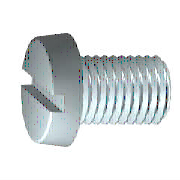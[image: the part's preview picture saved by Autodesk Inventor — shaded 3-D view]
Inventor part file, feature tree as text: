
AUTODESK INVENTOR PART (.ipt)
format: ipt  version: 2015 (Build 190159000, 159)  size: 181,248 bytes
history: native  units: mm (DEFAULTED — no unit token found)
features: sketch x2, extrude x1, plane x1
ambient origin geometry x7: Origin, YZ Plane, XZ Plane, X Axis, Y Axis, Z Axis, Center Point
bodies: Solid1 (feature_tree), Body (feature_tree)
feature tree (4):
  sketch  "Sketch2"  dims[d2=0.306825mm d3=2.0mm d4=3.0mm d5=2.729367mm d8=90.0deg d7=0.0mm d9=5.5mm d10=0.872665mm d11=0.8mm d12=5.5mm d14=0.1mm d15=15.0mm d16=0.0mm d17=0.270635mm d18=0.306825mm d19=0.85mm d20=0.0mm d36=45.0deg d37=0.0mm d39=0.0mm]
  extrude  "Slot"  Depth=15.0mm
  plane  "Work Plane1"
  sketch  "Sketch1"  dims[d0=16.0mm d1=15.0mm]
